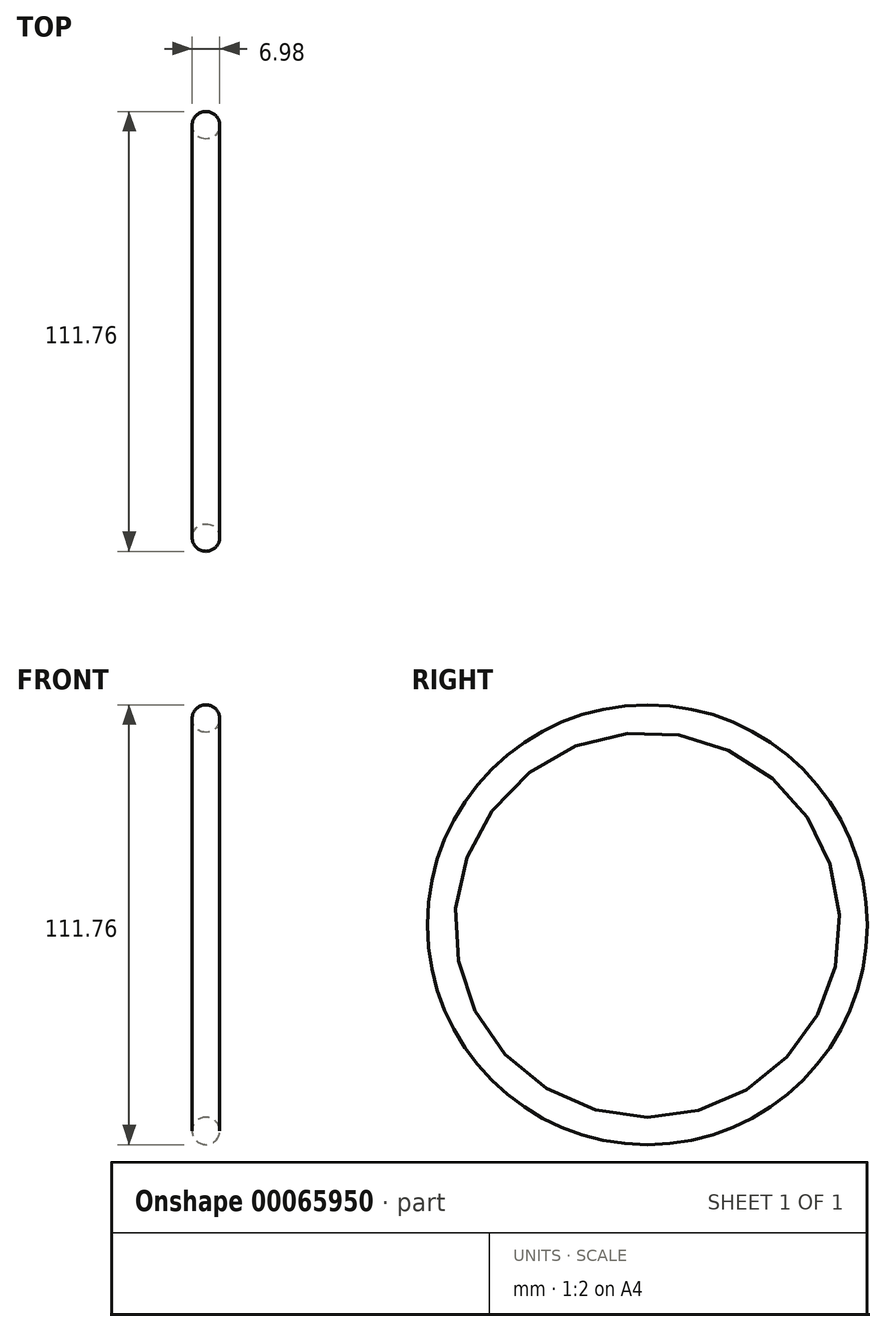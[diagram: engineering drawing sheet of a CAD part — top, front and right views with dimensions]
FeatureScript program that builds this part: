
annotation { "Feature Type Name" : "Feature", "Feature Type Description" : "" }
export const myFeature = defineFeature(function(context is Context, id is Id, definition is map)
    precondition{}
    {
        {
            var Q0;
            Q0=qCreatedBy(makeId("Front.planeOp"),FACE);
            var sketch = newSketch(context, id + "F0", { "sketchPlane" : qUnion([Q0])});
            skLineSegment(sketch, "E0", {"start": v(0, 0) * mm, "end": v(-6.06, 0) * mm, "construction": true});
            skCircle(sketch, "E1", {"center": v(0, 52.39) * mm, "radius": 3.5 * mm});
            skSolve(sketch);
        }
        {
            var Q0;
            Q0=makeQuery(id+"F0.imprint","IMPRINT",FACE,{"disambiguationData":[TD([[makeQuery(id+"F0.imprint","IMPRINT",EDGE,{"derivedFrom":sQuery(id+"F0.wireOp",EDGE,"E1")}),1.0]])]});
            var Q1;
            Q1=sQuery(id+"F0.wireOp",EDGE,"E0");
            revolve(context, id + "F1", {"entities" : qUnion([Q0]), "axis" : qUnion([Q1]), "revolveType" : RevolveType.FULL});
        }
    });
